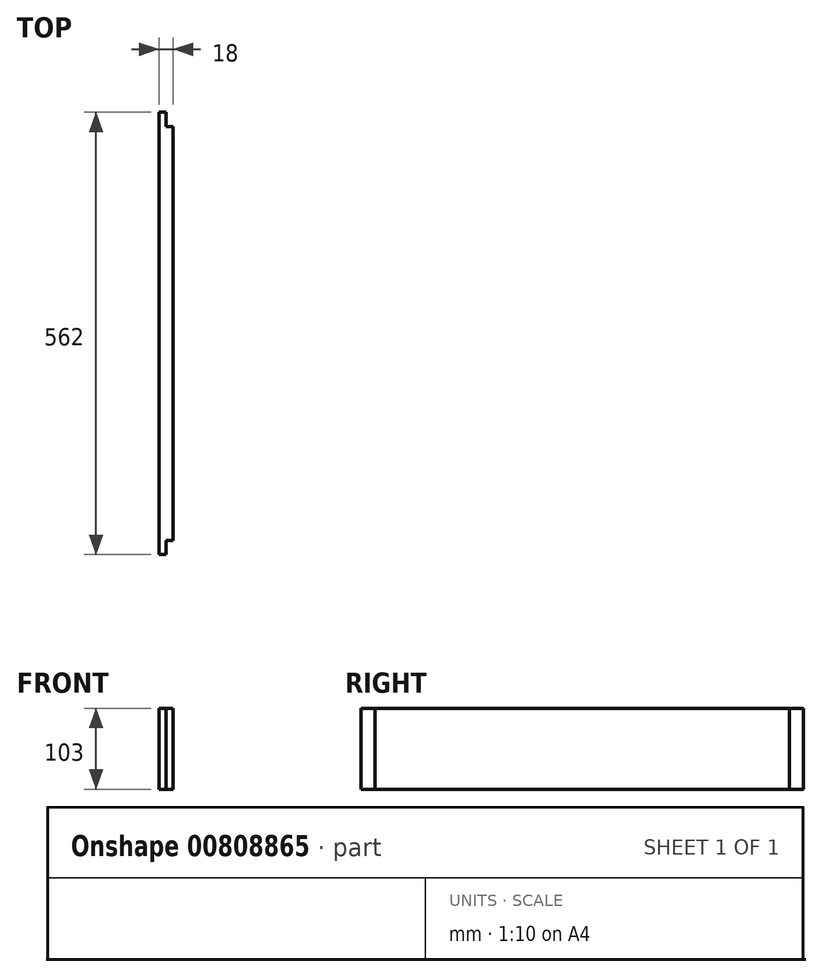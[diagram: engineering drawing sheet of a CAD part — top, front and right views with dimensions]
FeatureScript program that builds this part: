
annotation { "Feature Type Name" : "Feature", "Feature Type Description" : "" }
export const myFeature = defineFeature(function(context is Context, id is Id, definition is map)
    precondition{}
    {
        {
            var Q0;
            Q0=qCreatedBy(makeId("Right.planeOp"),FACE);
            var sketch = newSketch(context, id + "F0", { "sketchPlane" : qUnion([Q0])});
            skLineSegment(sketch, "E0.bottom", {"start": v(0, 0) * mm, "end": v(562, 0) * mm});
            skLineSegment(sketch, "E0.top", {"start": v(0, 103) * mm, "end": v(562, 103) * mm});
            skLineSegment(sketch, "E0.left", {"start": v(0, 0) * mm, "end": v(0, 103) * mm});
            skLineSegment(sketch, "E0.right", {"start": v(562, 0) * mm, "end": v(562, 103) * mm});
            skLineSegment(sketch, "E1.bottom", {"start": v(0, 103) * mm, "end": v(18, 103) * mm});
            skLineSegment(sketch, "E1.top", {"start": v(0, 0) * mm, "end": v(18, 0) * mm});
            skLineSegment(sketch, "E1.left", {"start": v(0, 103) * mm, "end": v(0, 0) * mm});
            skLineSegment(sketch, "E1.right", {"start": v(18, 103) * mm, "end": v(18, 0) * mm});
            skLineSegment(sketch, "E2.bottom", {"start": v(562, 103) * mm, "end": v(544, 103) * mm});
            skLineSegment(sketch, "E2.top", {"start": v(562, 0) * mm, "end": v(544, 0) * mm});
            skLineSegment(sketch, "E2.left", {"start": v(562, 103) * mm, "end": v(562, 0) * mm});
            skLineSegment(sketch, "E2.right", {"start": v(544, 103) * mm, "end": v(544, 0) * mm});
            skSolve(sketch);
        }
        {
            var Q0;
            {var subQ0=sQuery(id+"F0.wireOp",EDGE,"E1.right");Q0=makeQuery(id+"F0.imprint","IMPRINT",FACE,{"disambiguationData":[TD([[makeQuery(id+"F0.imprint","IMPRINT",EDGE,{"derivedFrom":subQ0}),1.0]])]});}
            extrude(context, id + "F1", {"entities" : qUnion([Q0]), "depth" : 18 * mm, "offsetDistance" : 25 * mm});
        }
        {
            var Q0;
            {var subQ2=sQuery(id+"F0.wireOp",EDGE,"E0.left");Q0=makeQuery(id+"F0.imprint","IMPRINT",FACE,{"disambiguationData":[TD([[makeQuery(id+"F0.imprint","IMPRINT",EDGE,{"derivedFrom":subQ2}),-1.0]])]});}
            var Q1;
            {var subQ0=sQuery(id+"F0.wireOp",EDGE,"E0.right");Q1=makeQuery(id+"F0.imprint","IMPRINT",FACE,{"disambiguationData":[TD([[makeQuery(id+"F0.imprint","IMPRINT",EDGE,{"derivedFrom":subQ0}),1.0]])]});}
            extrude(context, id + "F2", {"entities" : qUnion([Q0, Q1]), "operationType" : NewBodyOperationType.ADD, "depth" : 9 * mm, "offsetDistance" : 25 * mm});
        }
    });
